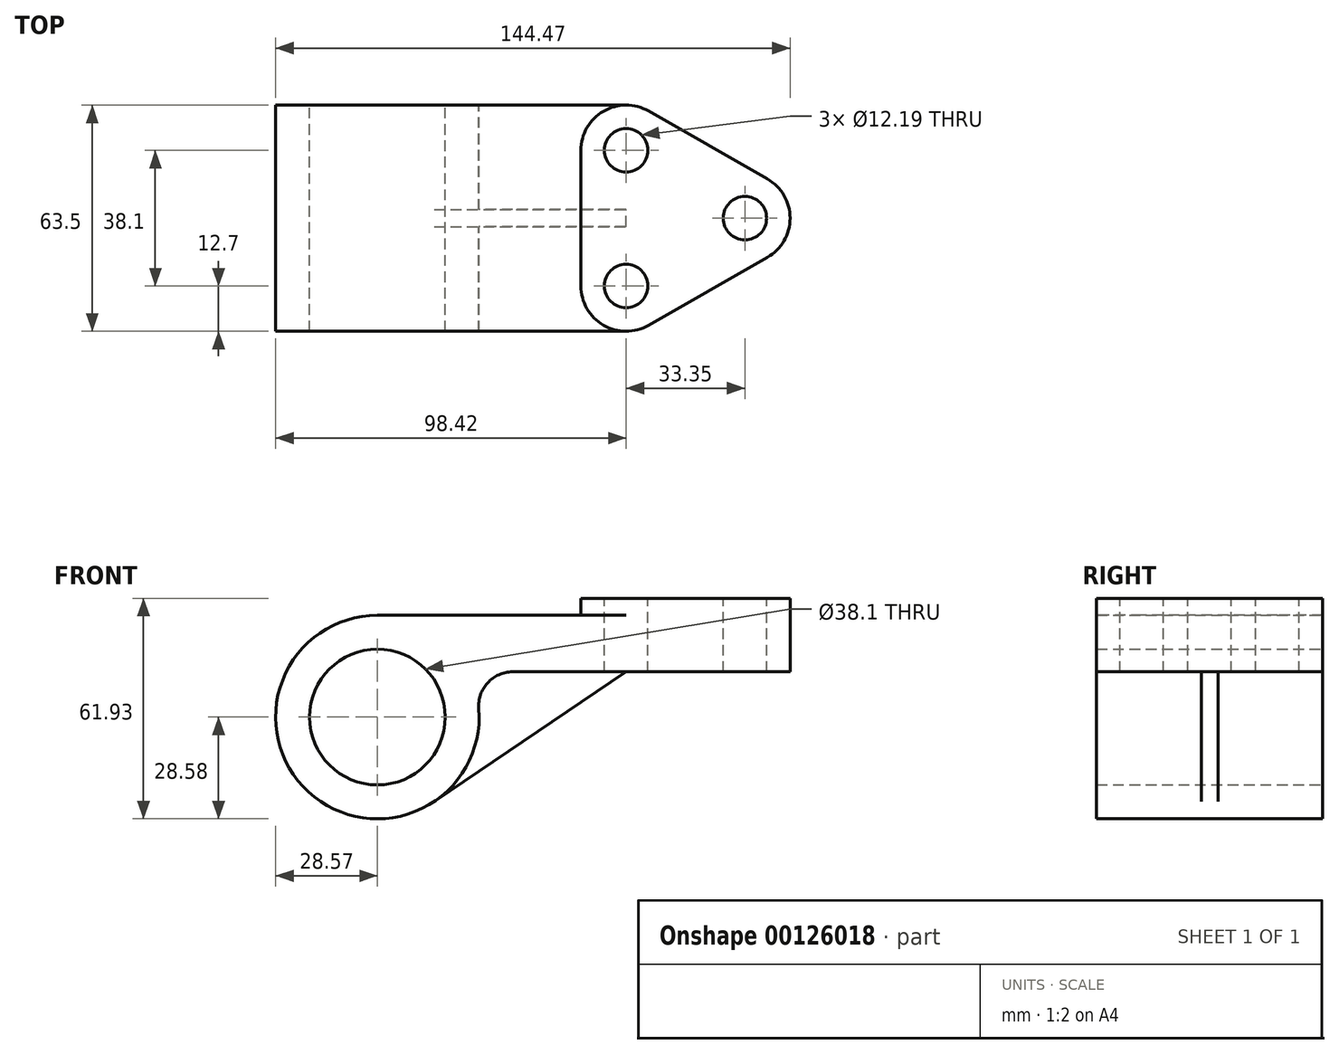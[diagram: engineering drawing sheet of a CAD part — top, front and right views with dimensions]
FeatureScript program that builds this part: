
annotation { "Feature Type Name" : "Feature", "Feature Type Description" : "" }
export const myFeature = defineFeature(function(context is Context, id is Id, definition is map)
    precondition{}
    {
        {
            var Q0;
            Q0=qCreatedBy(makeId("Front.planeOp"),FACE);
            var sketch = newSketch(context, id + "F0", { "sketchPlane" : qUnion([Q0])});
            skCircle(sketch, "E0", {"center": v(0, 0) * mm, "radius": 19.05 * mm});
            skArc(sketch, "E1", {"start": v(0, 28.58) * mm, "mid": v(-19.35, -21.03) * mm, "end": v(28.48, 2.38) * mm});
            skLineSegment(sketch, "E2", {"start": v(0, 28.58) * mm, "end": v(69.85, 28.58) * mm});
            skLineSegment(sketch, "E3", {"start": v(69.85, 28.58) * mm, "end": v(69.85, 12.7) * mm});
            skLineSegment(sketch, "E4", {"start": v(69.85, 12.7) * mm, "end": v(37.97, 12.7) * mm});
            skArc(sketch, "E5", {"start": v(37.97, 12.7) * mm, "mid": v(30.96, 9.62) * mm, "end": v(28.48, 2.38) * mm});
            skSolve(sketch);
        }
        {
            var Q0;
            Q0 = qSketchRegion(id + "F0", true);
            extrude(context, id + "F1", {"entities" : qUnion([Q0]), "depth" : 63.5 * mm});
        }
        {
            var Q0;
            Q0=makeQuery(id+"F1.opExtrude","SWEPT_FACE",FACE,{"disambiguationData":[OSD([sQuery(id+"F0.wireOp",EDGE,"E2")])]});
            var sketch = newSketch(context, id + "F2", { "sketchPlane" : qUnion([Q0])});
            skLineSegment(sketch, "E6", {"start": v(0, 0) * mm, "end": v(97.46, 0) * mm, "construction": true});
            skLineSegment(sketch, "E7", {"start": v(0, -31.75) * mm, "end": v(120, -31.75) * mm, "construction": true});
            skPoint(sketch, "E7.endSnap0", {"position": v(0, -31.75) * mm});
            skArc(sketch, "E8", {"start": v(69.85, 0) * mm, "mid": v(60.87, -3.72) * mm, "end": v(57.15, -12.7) * mm});
            skLineSegment(sketch, "E9", {"start": v(57.15, -12.7) * mm, "end": v(57.15, -31.75) * mm});
            skArc(sketch, "E10", {"start": v(76.15, -1.67) * mm, "mid": v(73.1, -0.43) * mm, "end": v(69.85, 0) * mm});
            skLineSegment(sketch, "E11", {"start": v(76.15, -1.67) * mm, "end": v(109.5, -20.72) * mm});
            skArc(sketch, "E12", {"start": v(115.9, -31.75) * mm, "mid": v(114.18, -25.37) * mm, "end": v(109.5, -20.72) * mm});
            skArc(sketch, "E13.MirrorCS", {"start": v(115.9, -31.75) * mm, "mid": v(114.18, -38.13) * mm, "end": v(109.5, -42.78) * mm});
            skLineSegment(sketch, "E14.MirrorCS", {"start": v(76.15, -61.83) * mm, "end": v(109.5, -42.78) * mm});
            skArc(sketch, "E15.MirrorCS", {"start": v(76.15, -61.83) * mm, "mid": v(73.1, -63.07) * mm, "end": v(69.85, -63.5) * mm});
            skLineSegment(sketch, "E16.MirrorCS", {"start": v(57.15, -50.8) * mm, "end": v(57.15, -31.75) * mm});
            skArc(sketch, "E17.MirrorCS", {"start": v(69.85, -63.5) * mm, "mid": v(60.87, -59.78) * mm, "end": v(57.15, -50.8) * mm});
            skSolve(sketch);
        }
        {
            var Q0;
            Q0 = qSketchRegion(id + "F2", true);
            var Q1;
            Q1=makeQuery(id+"F1.opExtrude","SWEPT_FACE",FACE,{"disambiguationData":[OSD([sQuery(id+"F0.wireOp",EDGE,"E4")])]});
            extrude(context, id + "F3", {"entities" : qUnion([Q0]), "operationType" : NewBodyOperationType.ADD, "endBound" : BoundingType.UP_TO_SURFACE, "oppositeDirection" : true, "endBoundEntityFace" : qUnion([Q1]), "depth" : 25.4 * mm, "hasSecondDirection" : true, "secondDirectionOppositeDirection" : false, "secondDirectionDepth" : 4.78 * mm});
        }
        {
            var Q0;
            Q0=makeQuery(id+"F3.opExtrude","CAP_FACE",FACE,{"disambiguationData":[OSD([sQuery(id+"F2.wireOp",EDGE,"E8"),sQuery(id+"F2.wireOp",EDGE,"E9"),sQuery(id+"F2.wireOp",EDGE,"E10"),sQuery(id+"F2.wireOp",EDGE,"E11"),sQuery(id+"F2.wireOp",EDGE,"E12"),sQuery(id+"F2.wireOp",EDGE,"E13.MirrorCS"),sQuery(id+"F2.wireOp",EDGE,"E14.MirrorCS"),sQuery(id+"F2.wireOp",EDGE,"E15.MirrorCS"),sQuery(id+"F2.wireOp",EDGE,"E16.MirrorCS"),sQuery(id+"F2.wireOp",EDGE,"E17.MirrorCS")])],"isStart":true});
            var sketch = newSketch(context, id + "F4", { "sketchPlane" : qUnion([Q0])});
            skCircle(sketch, "E18", {"center": v(69.85, -12.7) * mm, "radius": 6.1 * mm});
            skCircle(sketch, "E19", {"center": v(69.85, -50.8) * mm, "radius": 6.1 * mm});
            skCircle(sketch, "E20", {"center": v(103.2, -31.75) * mm, "radius": 6.1 * mm});
            skSolve(sketch);
        }
        {
            var Q0;
            Q0 = qSketchRegion(id + "F4", true);
            extrude(context, id + "F5", {"entities" : qUnion([Q0]), "operationType" : NewBodyOperationType.REMOVE, "endBound" : BoundingType.THROUGH_ALL, "oppositeDirection" : true, "depth" : 25.4 * mm});
        }
        {
            var Q0;
            Q0=qCreatedBy(makeId("Front.planeOp"),FACE);
            cPlane(context, id + "F6", {"entities" : qUnion([Q0]), "cplaneType" : CPlaneType.OFFSET, "offset" : 31.75 * mm, "width" : 152.4 * mm, "height" : 152.4 * mm});
        }
        {
            var Q0;
            Q0=qCreatedBy(id+"F6.planeOp",FACE);
            var sketch = newSketch(context, id + "F7", { "sketchPlane" : qUnion([Q0])});
            skLineSegment(sketch, "E21", {"start": v(16, -23.68) * mm, "end": v(69.85, 12.7) * mm});
            skArc(sketch, "E22.0", {"start": v(16, -23.68) * mm, "mid": v(25.77, -12.34) * mm, "end": v(28.48, 2.38) * mm});
            skArc(sketch, "E22.1", {"start": v(37.97, 12.7) * mm, "mid": v(30.96, 9.62) * mm, "end": v(28.48, 2.38) * mm});
            skLineSegment(sketch, "E22.2", {"start": v(69.85, 12.7) * mm, "end": v(37.97, 12.7) * mm});
            skPoint(sketch, "E23.orphan", {"position": v(0, 28.58) * mm});
            skSolve(sketch);
        }
        {
            var Q0;
            Q0 = qSketchRegion(id + "F7", true);
            extrude(context, id + "F8", {"entities" : qUnion([Q0]), "operationType" : NewBodyOperationType.ADD, "endBound" : BoundingType.SYMMETRIC, "depth" : 4.76 * mm});
        }
    });
